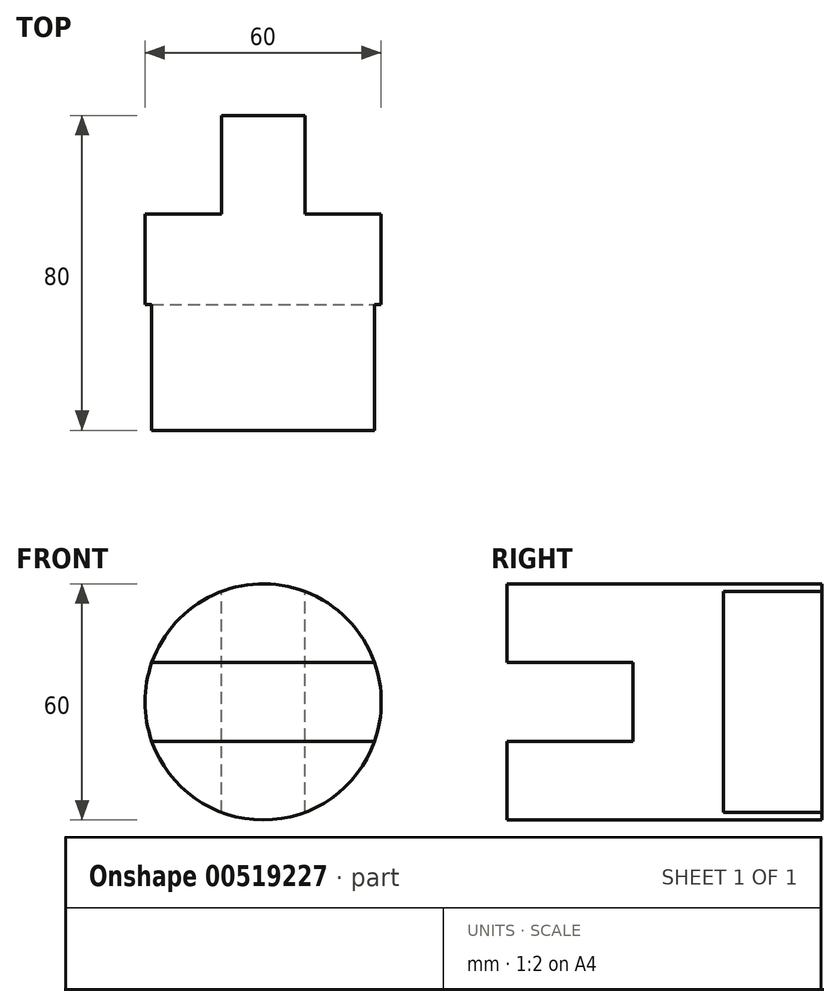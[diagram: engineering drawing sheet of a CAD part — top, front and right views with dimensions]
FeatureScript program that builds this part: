
annotation { "Feature Type Name" : "Feature", "Feature Type Description" : "" }
export const myFeature = defineFeature(function(context is Context, id is Id, definition is map)
    precondition{}
    {
        {
            var Q0;
            Q0=qCreatedBy(makeId("Front.planeOp"),FACE);
            var sketch = newSketch(context, id + "F0", { "sketchPlane" : qUnion([Q0])});
            skCircle(sketch, "E0", {"center": v(0, 0) * mm, "radius": 30 * mm});
            skSolve(sketch);
        }
        {
            var Q0;
            Q0=makeQuery(id+"F0.imprint","IMPRINT",FACE,{"disambiguationData":[TD([[makeQuery(id+"F0.imprint","IMPRINT",EDGE,{"derivedFrom":sQuery(id+"F0.wireOp",EDGE,"E0")}),1.0]])]});
            extrude(context, id + "F1", {"entities" : qUnion([Q0]), "endBound" : BoundingType.SYMMETRIC, "depth" : 80 * mm, "offsetDistance" : 25 * mm});
        }
        {
            var Q0;
            Q0=makeQuery(id+"F1.opExtrude","CAP_FACE",FACE,{"disambiguationData":[OSD([sQuery(id+"F0.wireOp",EDGE,"E0")])],"isStart":false});
            var sketch = newSketch(context, id + "F2", { "sketchPlane" : qUnion([Q0])});
            skLineSegment(sketch, "E1", {"start": v(-30, 0) * mm, "end": v(30, 0) * mm, "construction": true});
            skLineSegment(sketch, "E2", {"start": v(-28.28, 10) * mm, "end": v(28.28, 10) * mm});
            skLineSegment(sketch, "E3", {"start": v(-28.28, -10) * mm, "end": v(28.28, -10) * mm});
            skArc(sketch, "E4.0", {"start": v(-28.28, 10) * mm, "mid": v(-30, 0) * mm, "end": v(-28.28, -10) * mm});
            skArc(sketch, "E5.trimOffspring", {"start": v(28.28, -10) * mm, "mid": v(30, 0) * mm, "end": v(28.28, 10) * mm});
            skSolve(sketch);
        }
        {
            var Q0;
            Q0=makeQuery(id+"F2.imprint","IMPRINT",FACE,{"disambiguationData":[TD([[makeQuery(id+"F2.imprint","IMPRINT",EDGE,{"derivedFrom":sQuery(id+"F2.wireOp",EDGE,"E2")}),-1.0]])]});
            extrude(context, id + "F3", {"entities" : qUnion([Q0]), "operationType" : NewBodyOperationType.REMOVE, "oppositeDirection" : true, "depth" : 32 * mm, "offsetDistance" : 25 * mm});
        }
        {
            var Q0;
            Q0=makeQuery(id+"F1.opExtrude","CAP_FACE",FACE,{"disambiguationData":[OSD([sQuery(id+"F0.wireOp",EDGE,"E0")])],"isStart":true});
            var sketch = newSketch(context, id + "F4", { "sketchPlane" : qUnion([Q0])});
            skLineSegment(sketch, "E6", {"start": v(0, -30) * mm, "end": v(0, 30) * mm, "construction": true});
            skLineSegment(sketch, "E7", {"start": v(10.58, -28.07) * mm, "end": v(10.58, 28.07) * mm});
            skLineSegment(sketch, "E8", {"start": v(-10.58, -28.07) * mm, "end": v(-10.58, 28.07) * mm});
            skSolve(sketch);
        }
        {
            var Q0;
            {var subQ0=sQuery(id+"F4.wireOp",EDGE,"E7");Q0=makeQuery(id+"F4.imprint","IMPRINT",FACE,{"disambiguationData":[TD([[makeQuery(id+"F4.imprint","IMPRINT",EDGE,{"derivedFrom":subQ0}),-1.0]])]});}
            var Q1;
            {var subQ0=sQuery(id+"F4.wireOp",EDGE,"E8");Q1=makeQuery(id+"F4.imprint","IMPRINT",FACE,{"disambiguationData":[TD([[makeQuery(id+"F4.imprint","IMPRINT",EDGE,{"derivedFrom":subQ0}),1.0]])]});}
            extrude(context, id + "F5", {"entities" : qUnion([Q0, Q1]), "operationType" : NewBodyOperationType.REMOVE, "oppositeDirection" : true, "depth" : 25 * mm, "offsetDistance" : 25 * mm});
        }
    });
